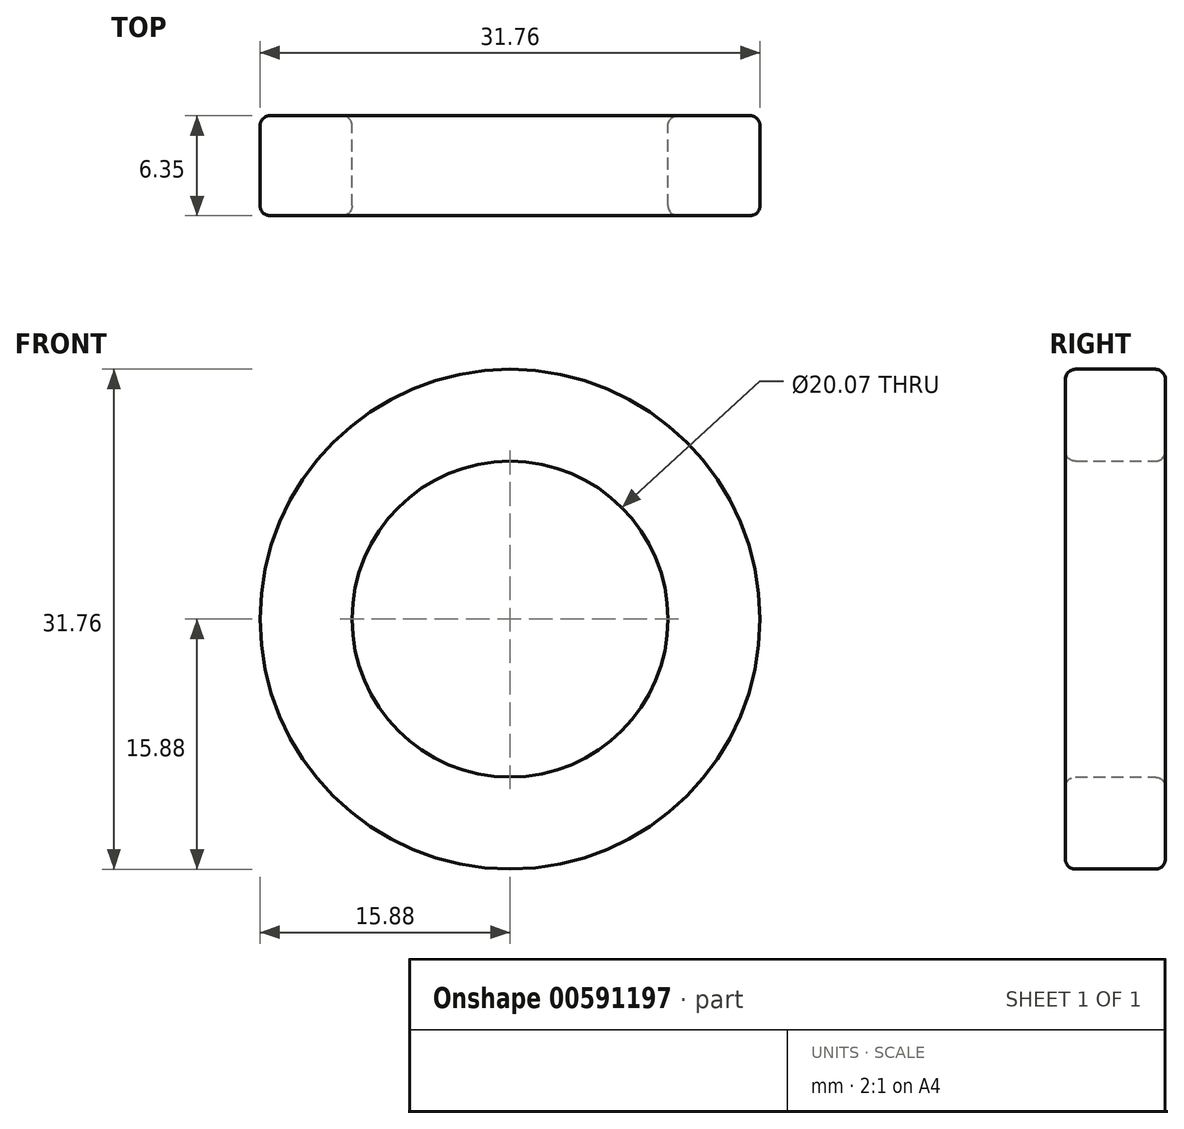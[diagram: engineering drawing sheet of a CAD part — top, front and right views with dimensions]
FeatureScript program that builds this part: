
annotation { "Feature Type Name" : "Feature", "Feature Type Description" : "" }
export const myFeature = defineFeature(function(context is Context, id is Id, definition is map)
    precondition{}
    {
        {
            var Q0;
            Q0=qCreatedBy(makeId("Front.planeOp"),FACE);
            var sketch = newSketch(context, id + "F0", { "sketchPlane" : qUnion([Q0])});
            skCircle(sketch, "E0", {"center": v(0, 0) * mm, "radius": 15.88 * mm});
            skCircle(sketch, "E1", {"center": v(0, 0) * mm, "radius": 10.03 * mm});
            skSolve(sketch);
        }
        {
            var Q0;
            Q0=makeQuery(id+"F0.imprint","IMPRINT",FACE,{"disambiguationData":[TD([[makeQuery(id+"F0.imprint","IMPRINT",EDGE,{"derivedFrom":sQuery(id+"F0.wireOp",EDGE,"E0")}),1.0]])]});
            extrude(context, id + "F1", {"entities" : qUnion([Q0]), "depth" : 6.35 * mm, "offsetDistance" : 25.4 * mm});
        }
        {
            var Q0;
            Q0=makeQuery(id+"F1.opExtrude","CAP_EDGE",EDGE,{"disambiguationData":[OSD([sQuery(id+"F0.wireOp",EDGE,"E1")])],"isStart":false});
            var Q1;
            Q1=makeQuery(id+"F1.opExtrude","CAP_EDGE",EDGE,{"disambiguationData":[OSD([sQuery(id+"F0.wireOp",EDGE,"E1")])],"isStart":true});
            var Q2;
            Q2=makeQuery(id+"F1.opExtrude","CAP_EDGE",EDGE,{"disambiguationData":[OSD([sQuery(id+"F0.wireOp",EDGE,"E0")])],"isStart":false});
            var Q3;
            Q3=makeQuery(id+"F1.opExtrude","CAP_EDGE",EDGE,{"disambiguationData":[OSD([sQuery(id+"F0.wireOp",EDGE,"E0")])],"isStart":true});
            fillet(context, id + "F2", {"entities" : qUnion([Q0, Q1, Q2, Q3]), "radius" : 0.64 * mm, "tangentPropagation" : true, "allowEdgeOverflow" : false});
        }
    });
